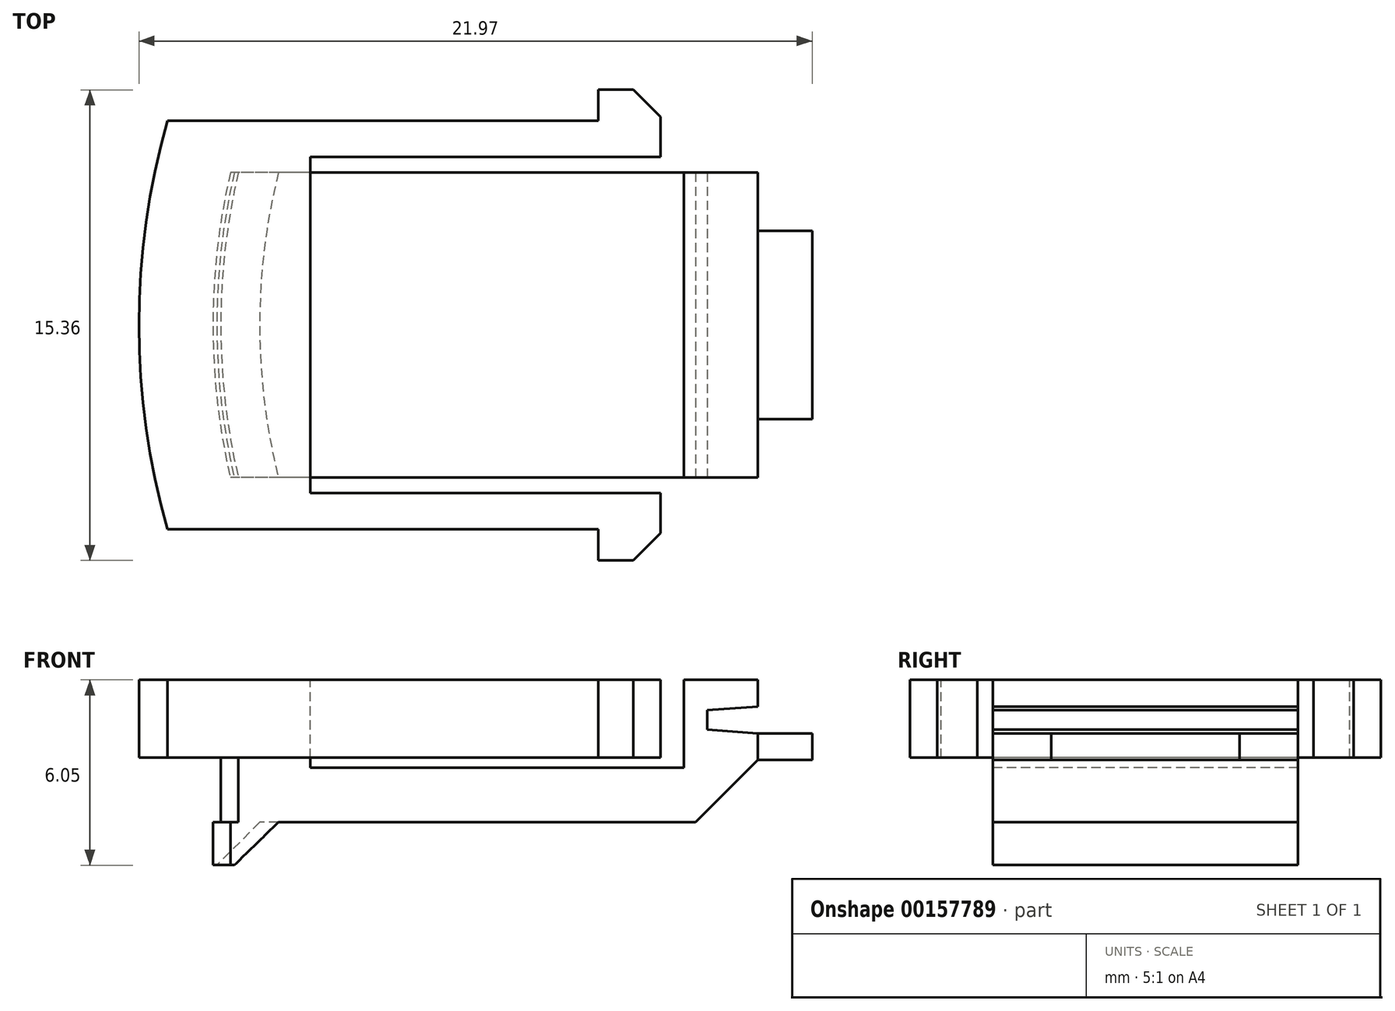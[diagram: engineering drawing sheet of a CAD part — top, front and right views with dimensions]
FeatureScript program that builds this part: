
annotation { "Feature Type Name" : "Feature", "Feature Type Description" : "" }
export const myFeature = defineFeature(function(context is Context, id is Id, definition is map)
    precondition{}
    {
        {
            var Q0;
            Q0=qCreatedBy(makeId("Top.planeOp"),FACE);
            var sketch = newSketch(context, id + "F0", { "sketchPlane" : qUnion([Q0])});
            skLineSegment(sketch, "E0", {"start": v(-4.34, 0) * mm, "end": v(-4.34, 4.98) * mm});
            skLineSegment(sketch, "E1", {"start": v(-4.34, 4.98) * mm, "end": v(-21.3, 4.98) * mm});
            skArc(sketch, "E2", {"start": v(-21.3, 4.98) * mm, "mid": v(-21.73, 2.5) * mm, "end": v(-21.87, 0) * mm});
            skLineSegment(sketch, "E3", {"start": v(-4.34, 0) * mm, "end": v(-21.87, 0) * mm});
            skLineSegment(sketch, "E4", {"start": v(-4.34, 0) * mm, "end": v(7.92, 0) * mm, "construction": true});
            skSolve(sketch);
        }
        {
            var Q0;
            Q0 = qSketchRegion(id + "F0", true);
            extrude(context, id + "F1", {"entities" : qUnion([Q0]), "depth" : 4.65 * mm});
        }
        {
            var Q0;
            Q0=makeQuery(id+"F1.opExtrude","CAP_EDGE",EDGE,{"disambiguationData":[OSD([sQuery(id+"F0.wireOp",EDGE,"E0")])],"isStart":true});
            chamfer(context, id + "F2", {"entities" : qUnion([Q0]), "width" : 2.03 * mm, "tangentPropagation" : true});
        }
        {
            var Q0;
            Q0=makeQuery(id+"F1.opExtrude","SWEPT_FACE",FACE,{"disambiguationData":[OSD([sQuery(id+"F0.wireOp",EDGE,"E3")])]});
            var sketch = newSketch(context, id + "F3", { "sketchPlane" : qUnion([Q0])});
            skLineSegment(sketch, "E5", {"start": v(-6.76, 4.65) * mm, "end": v(-6.76, 1.78) * mm});
            skLineSegment(sketch, "E6", {"start": v(-6.76, 1.78) * mm, "end": v(-18.95, 1.78) * mm});
            skLineSegment(sketch, "E7", {"start": v(-18.95, 1.78) * mm, "end": v(-18.95, 4.65) * mm});
            skLineSegment(sketch, "E8", {"start": v(-6.76, 4.65) * mm, "end": v(-18.95, 4.65) * mm});
            skSolve(sketch);
        }
        {
            var Q0;
            Q0 = qSketchRegion(id + "F3", true);
            extrude(context, id + "F4", {"entities" : qUnion([Q0]), "operationType" : NewBodyOperationType.REMOVE, "endBound" : BoundingType.THROUGH_ALL, "oppositeDirection" : true, "depth" : 25.4 * mm});
        }
        {
            var Q0;
            Q0=makeQuery(id+"F1.opExtrude","CAP_FACE",FACE,{"disambiguationData":[OSD([sQuery(id+"F0.wireOp",EDGE,"E0"),sQuery(id+"F0.wireOp",EDGE,"E1"),sQuery(id+"F0.wireOp",EDGE,"E2"),sQuery(id+"F0.wireOp",EDGE,"E3")])],"isStart":true});
            var sketch = newSketch(context, id + "F5", { "sketchPlane" : qUnion([Q0])});
            skArc(sketch, "E9.0", {"start": v(-21.56, -4.98) * mm, "mid": v(-21.98, -2.5) * mm, "end": v(-22.12, 0) * mm});
            skArc(sketch, "E10.0", {"start": v(-19.99, -4.98) * mm, "mid": v(-20.45, -2.5) * mm, "end": v(-20.6, 0) * mm});
            skLineSegment(sketch, "E11", {"start": v(-20.6, 0) * mm, "end": v(-22.12, 0) * mm});
            skLineSegment(sketch, "E12", {"start": v(-19.99, -4.98) * mm, "end": v(-21.56, -4.98) * mm});
            skSolve(sketch);
        }
        {
            var Q0;
            Q0 = qSketchRegion(id + "F5", true);
            extrude(context, id + "F6", {"entities" : qUnion([Q0]), "operationType" : NewBodyOperationType.ADD, "depth" : 1.4 * mm});
        }
        {
            var Q0;
            Q0=makeQuery(id+"F6.opExtrude","CAP_EDGE",EDGE,{"disambiguationData":[OSD([sQuery(id+"F5.wireOp",EDGE,"E10.0")])],"isStart":false});
            chamfer(context, id + "F7", {"entities" : qUnion([Q0]), "width" : 1.4 * mm, "tangentPropagation" : true});
        }
        {
            var Q0;
            Q0=makeQuery(id+"F6.boolean.opBoolean","MERGE",FACE,{"derivedFrom":[makeQuery(id+"F1.opExtrude","SWEPT_FACE",FACE,{"disambiguationData":[OSD([sQuery(id+"F0.wireOp",EDGE,"E3")])]}),makeQuery(id+"F6.opExtrude","SWEPT_FACE",FACE,{"disambiguationData":[OSD([sQuery(id+"F5.wireOp",EDGE,"E11")])]})]});
            var sketch = newSketch(context, id + "F8", { "sketchPlane" : qUnion([Q0])});
            skLineSegment(sketch, "E13", {"start": v(-4.34, 4.65) * mm, "end": v(-4.34, 3.78) * mm, "construction": true});
            skLineSegment(sketch, "E14", {"start": v(-4.34, 3.78) * mm, "end": v(-4.34, 2.9) * mm});
            skLineSegment(sketch, "E15", {"start": v(-4.34, 2.9) * mm, "end": v(-4.34, 2.03) * mm, "construction": true});
            skLineSegment(sketch, "E16", {"start": v(-4.34, 2.9) * mm, "end": v(-6, 3.02) * mm});
            skLineSegment(sketch, "E17", {"start": v(-6, 3.02) * mm, "end": v(-6, 3.66) * mm});
            skLineSegment(sketch, "E18", {"start": v(-6, 3.66) * mm, "end": v(-4.34, 3.78) * mm});
            skSolve(sketch);
        }
        {
            var Q0;
            Q0 = qSketchRegion(id + "F8", true);
            extrude(context, id + "F9", {"entities" : qUnion([Q0]), "operationType" : NewBodyOperationType.REMOVE, "endBound" : BoundingType.THROUGH_ALL, "oppositeDirection" : true, "depth" : 25.4 * mm});
        }
        {
            var Q0;
            {var subQ0=sQuery(id+"F0.wireOp",EDGE,"E0");Q0=makeQuery(id+"F9.boolean.opBoolean","SPLIT",FACE,{"disambiguationData":[TD([makeQuery(id+"F2.opChamfer","BLEND_FACE",FACE,{"disambiguationData":[OSD([subQ0])]})])],"derivedFrom":makeQuery(id+"F1.opExtrude","SWEPT_FACE",FACE,{"disambiguationData":[OSD([subQ0])]})});}
            var sketch = newSketch(context, id + "F10", { "sketchPlane" : qUnion([Q0])});
            skLineSegment(sketch, "E19.bottom", {"start": v(0, 2.9) * mm, "end": v(3.07, 2.9) * mm});
            skLineSegment(sketch, "E19.top", {"start": v(0, 2.03) * mm, "end": v(3.07, 2.03) * mm});
            skLineSegment(sketch, "E19.left", {"start": v(0, 2.9) * mm, "end": v(0, 2.03) * mm});
            skLineSegment(sketch, "E19.right", {"start": v(3.07, 2.9) * mm, "end": v(3.07, 2.03) * mm});
            skSolve(sketch);
        }
        {
            var Q0;
            Q0 = qSketchRegion(id + "F10", true);
            extrude(context, id + "F11", {"entities" : qUnion([Q0]), "operationType" : NewBodyOperationType.ADD, "depth" : 1.78 * mm});
        }
        {
            var Q0;
            {var subQ0=sQuery(id+"F0.wireOp",EDGE,"E1");var subQ1=sQuery(id+"F0.wireOp",EDGE,"E2");var subQ2=sQuery(id+"F0.wireOp",EDGE,"E3");Q0=makeQuery(id+"F4.boolean.opBoolean","SPLIT",FACE,{"disambiguationData":[TD([makeQuery(id+"F1.opExtrude","SWEPT_FACE",FACE,{"disambiguationData":[OSD([subQ1])]})])],"derivedFrom":makeQuery(id+"F1.opExtrude","CAP_FACE",FACE,{"disambiguationData":[OSD([sQuery(id+"F0.wireOp",EDGE,"E0"),subQ0,subQ1,subQ2])],"isStart":false})});}
            var sketch = newSketch(context, id + "F12", { "sketchPlane" : qUnion([Q0])});
            skLineSegment(sketch, "E20", {"start": v(-18.95, 0) * mm, "end": v(-18.95, 5.49) * mm});
            skLineSegment(sketch, "E21", {"start": v(-18.95, 5.49) * mm, "end": v(-7.52, 5.49) * mm});
            skLineSegment(sketch, "E22", {"start": v(-7.52, 5.49) * mm, "end": v(-7.52, 7.68) * mm});
            skLineSegment(sketch, "E23", {"start": v(-18.95, 0) * mm, "end": v(-24.54, 0) * mm});
            skArc(sketch, "E24", {"start": v(-23.61, 6.67) * mm, "mid": v(-24.3, 3.37) * mm, "end": v(-24.54, 0) * mm});
            skLineSegment(sketch, "E25", {"start": v(-23.61, 6.67) * mm, "end": v(-9.55, 6.67) * mm});
            skLineSegment(sketch, "E26", {"start": v(-9.55, 6.67) * mm, "end": v(-9.55, 7.68) * mm});
            skLineSegment(sketch, "E27", {"start": v(-9.55, 7.68) * mm, "end": v(-7.52, 7.68) * mm});
            skLineSegment(sketch, "E28", {"start": v(-18.95, 0) * mm, "end": v(-14.82, 0) * mm, "construction": true});
            skSolve(sketch);
        }
        {
            var Q0;
            Q0 = qSketchRegion(id + "F12", true);
            extrude(context, id + "F13", {"entities" : qUnion([Q0]), "operationType" : NewBodyOperationType.ADD, "oppositeDirection" : true, "depth" : 2.54 * mm});
        }
        {
            var Q0;
            Q0=makeQuery(id+"F13.opExtrude","SWEPT_EDGE",EDGE,{"disambiguationData":[OSD([sQuery(id+"F12.wireOp",EDGE,"E22"),sQuery(id+"F12.wireOp",EDGE,"E27")])]});
            chamfer(context, id + "F14", {"entities" : qUnion([Q0]), "width" : 0.89 * mm, "tangentPropagation" : true});
        }
        {
            var Q0;
            Q0=makeQuery(id+"F1.opExtrude","SWEPT_BODY",BODY,{"disambiguationData":[OSD([sQuery(id+"F0.wireOp",EDGE,"E0"),sQuery(id+"F0.wireOp",EDGE,"E1"),sQuery(id+"F0.wireOp",EDGE,"E2"),sQuery(id+"F0.wireOp",EDGE,"E3")])]});
            var Q1;
            Q1=makeQuery(id+"F13.boolean.opBoolean","MERGE",FACE,{"derivedFrom":[makeQuery(id+"F11.boolean.opBoolean","MERGE",FACE,{"derivedFrom":[makeQuery(id+"F6.boolean.opBoolean","MERGE",FACE,{"derivedFrom":[makeQuery(id+"F1.opExtrude","SWEPT_FACE",FACE,{"disambiguationData":[OSD([sQuery(id+"F0.wireOp",EDGE,"E3")])]}),makeQuery(id+"F6.opExtrude","SWEPT_FACE",FACE,{"disambiguationData":[OSD([sQuery(id+"F5.wireOp",EDGE,"E11")])]})]}),makeQuery(id+"F11.opExtrude","SWEPT_FACE",FACE,{"disambiguationData":[OSD([sQuery(id+"F10.wireOp",EDGE,"E19.left")])]})]}),makeQuery(id+"F13.opExtrude","SWEPT_FACE",FACE,{"disambiguationData":[OSD([sQuery(id+"F12.wireOp",EDGE,"E23")])]})]});
            mirror(context, id + "F15", {"operationType" : NewBodyOperationType.ADD, "entities" : qUnion([Q0]), "mirrorPlane" : qUnion([Q1])});
        }
    });
